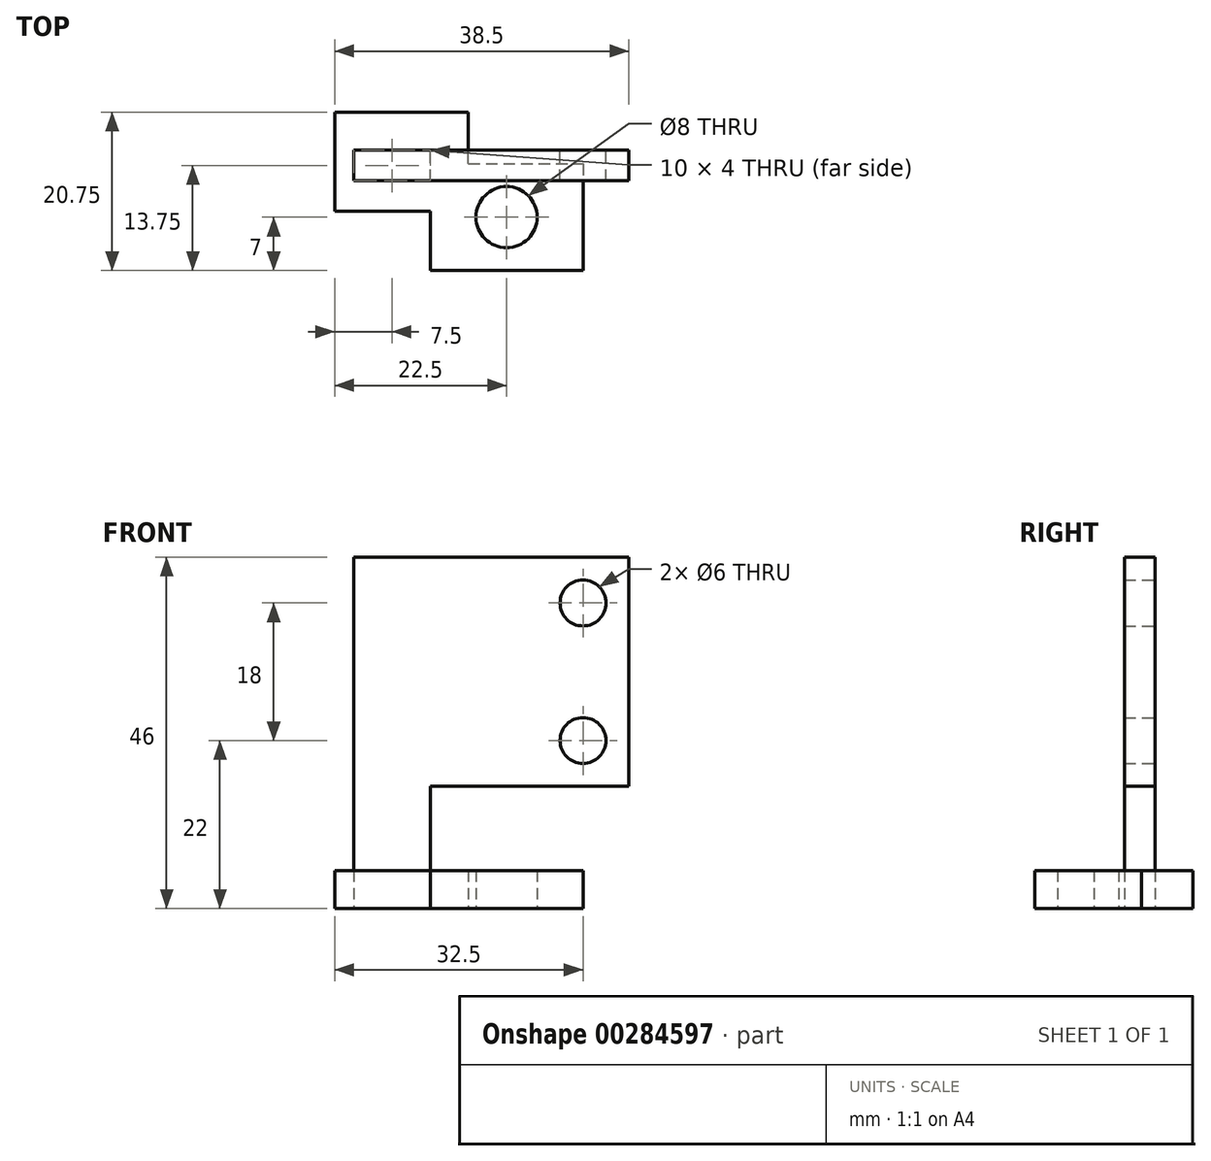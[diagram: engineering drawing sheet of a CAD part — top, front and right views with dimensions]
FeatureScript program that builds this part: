
annotation { "Feature Type Name" : "Feature", "Feature Type Description" : "" }
export const myFeature = defineFeature(function(context is Context, id is Id, definition is map)
    precondition{}
    {
        {
            var Q0;
            Q0=qCreatedBy(makeId("Top.planeOp"),FACE);
            var sketch = newSketch(context, id + "F0", { "sketchPlane" : qUnion([Q0])});
            skCircle(sketch, "E0", {"center": v(0, 0) * mm, "radius": 4 * mm});
            skLineSegment(sketch, "E1.bottom", {"start": v(-5, 7) * mm, "end": v(10, 7) * mm});
            skLineSegment(sketch, "E1.top", {"start": v(-10, -7) * mm, "end": v(10, -7) * mm});
            skLineSegment(sketch, "E1.right", {"start": v(10, 7) * mm, "end": v(10, -7) * mm});
            skLineSegment(sketch, "E2.bottom", {"start": v(-10, 8.75) * mm, "end": v(-20, 8.75) * mm});
            skLineSegment(sketch, "E2.top", {"start": v(-10, 4.75) * mm, "end": v(-20, 4.75) * mm});
            skLineSegment(sketch, "E2.left", {"start": v(-10, 8.75) * mm, "end": v(-10, 4.75) * mm});
            skLineSegment(sketch, "E2.right", {"start": v(-20, 8.75) * mm, "end": v(-20, 4.75) * mm});
            skLineSegment(sketch, "E3.bottom", {"start": v(-10, 0.75) * mm, "end": v(-22.5, 0.75) * mm});
            skLineSegment(sketch, "E3.top", {"start": v(-5, 13.75) * mm, "end": v(-22.5, 13.75) * mm});
            skLineSegment(sketch, "E3.left", {"start": v(-5, 7) * mm, "end": v(-5, 13.75) * mm});
            skLineSegment(sketch, "E3.right", {"start": v(-22.5, 0.75) * mm, "end": v(-22.5, 13.75) * mm});
            skLineSegment(sketch, "E4.trimOffspring", {"start": v(-10, 0.75) * mm, "end": v(-10, -7) * mm});
            skSolve(sketch);
        }
        {
            var Q0;
            Q0=qSketchRegion(id+"F0",true);
            extrude(context, id + "F1", {"entities" : qUnion([Q0]), "depth" : 5 * mm});
        }
        {
            var Q0;
            Q0=makeQuery(id+"F1.opExtrude","SWEPT_FACE",FACE,{"disambiguationData":[OSD([sQuery(id+"F0.wireOp",EDGE,"E2.bottom")])]});
            var sketch = newSketch(context, id + "F2", { "sketchPlane" : qUnion([Q0])});
            skLineSegment(sketch, "E5.bottom", {"start": v(-20, 0) * mm, "end": v(-10, 0) * mm});
            skLineSegment(sketch, "E5.top", {"start": v(-20, 46) * mm, "end": v(-10, 46) * mm});
            skLineSegment(sketch, "E5.left", {"start": v(-20, 0) * mm, "end": v(-20, 46) * mm});
            skLineSegment(sketch, "E5.right", {"start": v(-10, 0) * mm, "end": v(-10, 16) * mm});
            skLineSegment(sketch, "E6.bottom", {"start": v(-20, 46) * mm, "end": v(16, 46) * mm});
            skLineSegment(sketch, "E6.top", {"start": v(-10, 16) * mm, "end": v(16, 16) * mm});
            skLineSegment(sketch, "E6.left", {"start": v(-20, 46) * mm, "end": v(-20, 16) * mm});
            skLineSegment(sketch, "E6.right", {"start": v(16, 46) * mm, "end": v(16, 16) * mm});
            skCircle(sketch, "E7", {"center": v(10, 40) * mm, "radius": 3 * mm});
            skCircle(sketch, "E8", {"center": v(10, 22) * mm, "radius": 3 * mm});
            skLineSegment(sketch, "E9", {"start": v(10, 46) * mm, "end": v(10, 43) * mm, "construction": true});
            skLineSegment(sketch, "E10.trimOffspring", {"start": v(10, 37) * mm, "end": v(10, 25) * mm, "construction": true});
            skLineSegment(sketch, "E11.trimOffspring", {"start": v(10, 19) * mm, "end": v(10, 16) * mm, "construction": true});
            skSolve(sketch);
        }
        {
            var Q0;
            Q0=qSketchRegion(id+"F2",true);
            extrude(context, id + "F3", {"entities" : qUnion([Q0]), "depth" : 4 * mm});
        }
    });
